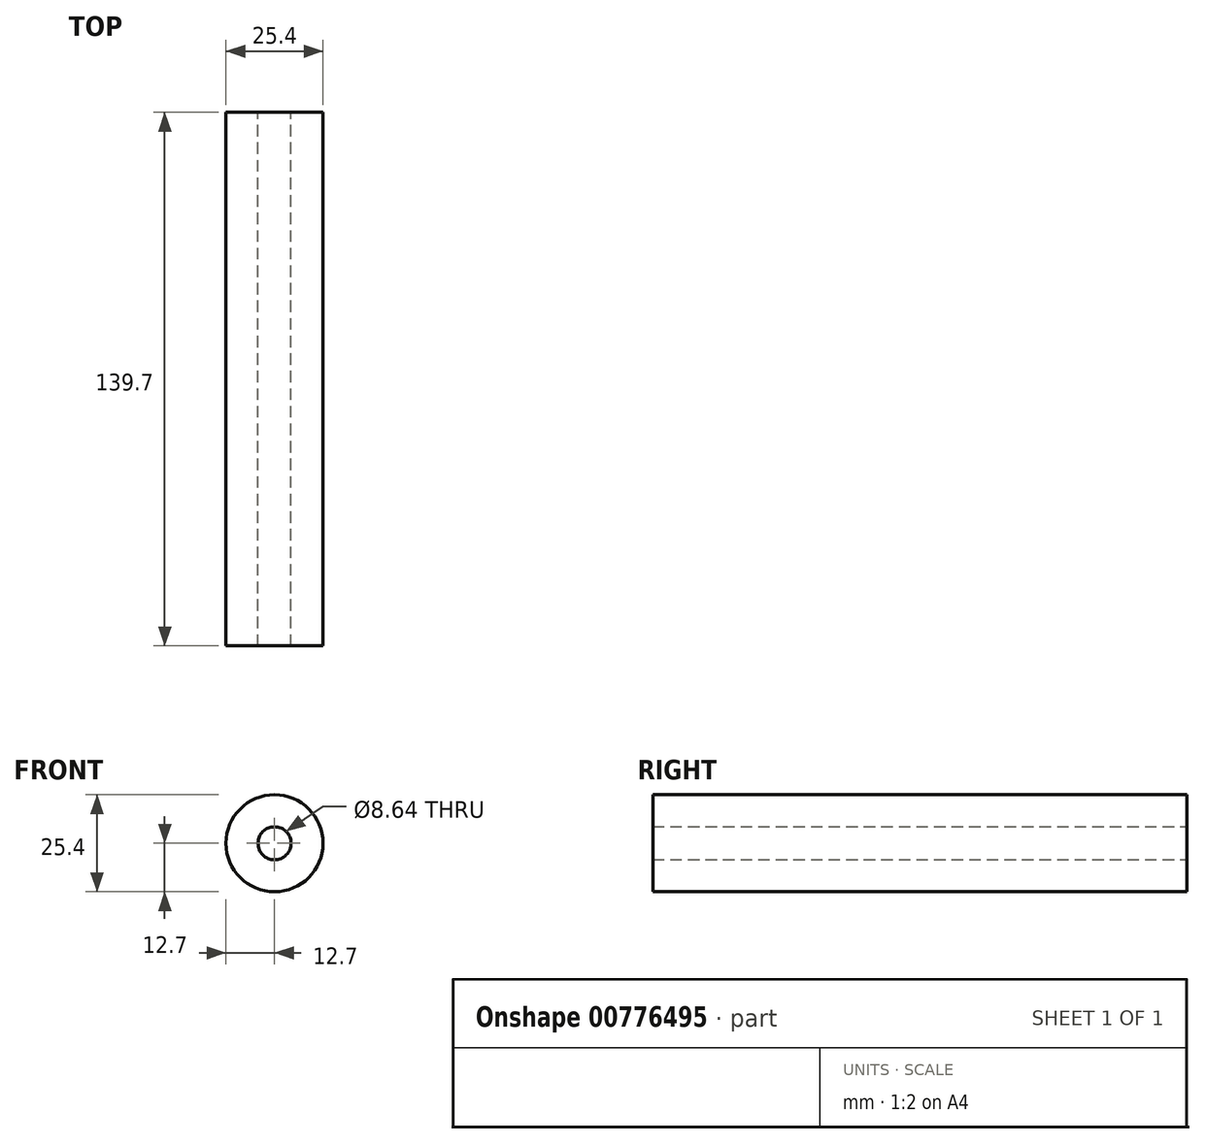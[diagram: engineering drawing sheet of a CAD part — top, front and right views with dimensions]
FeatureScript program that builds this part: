
annotation { "Feature Type Name" : "Feature", "Feature Type Description" : "" }
export const myFeature = defineFeature(function(context is Context, id is Id, definition is map)
    precondition{}
    {
        {
            var Q0;
            Q0=qCreatedBy(makeId("Front.planeOp"),FACE);
            var sketch = newSketch(context, id + "F0", { "sketchPlane" : qUnion([Q0])});
            skCircle(sketch, "E0", {"center": v(0, 0) * mm, "radius": 4.32 * mm});
            skCircle(sketch, "E1", {"center": v(0, 0) * mm, "radius": 12.7 * mm});
            skSolve(sketch);
        }
        {
            var Q0;
            Q0=qSketchRegion(id+"F0",true);
            extrude(context, id + "F1", {"entities" : qUnion([Q0]), "depth" : 139.7 * mm, "offsetDistance" : 25.4 * mm});
        }
    });
